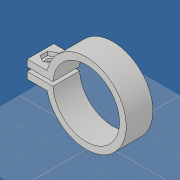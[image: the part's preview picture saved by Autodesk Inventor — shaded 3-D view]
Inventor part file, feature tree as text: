
AUTODESK INVENTOR PART (.ipt)
format: ipt  version: 2019 (Build 230136000, 136)  size: 121,856 bytes
history: native  units: mm
features: extrude x3, sketch x2
ambient origin geometry x8: Origin, YZ Plane, XZ Plane, XY Plane, X Axis, Y Axis, Z Axis, Center Point
bodies: Volumenkörper1 (feature_tree)
feature tree (5):
  extrude  "Extrusion1"  Depth=60.0mm
  sketch  "Skizze2"  dims[d2=5.0mm d4=3.0mm d5=15.0mm d6=20.0mm d7=0.0mm d8=10.0mm d9=6.5mm d10=20.0mm d11=0.0mm d12=3.0mm d13=0.0mm]
  extrude  "Extrusion2"  Depth=3.0mm
  extrude  "Extrusion3"  Depth=3.0mm
  sketch  "Skizze1"  dims[d0=50.0mm d1=60.0mm]
